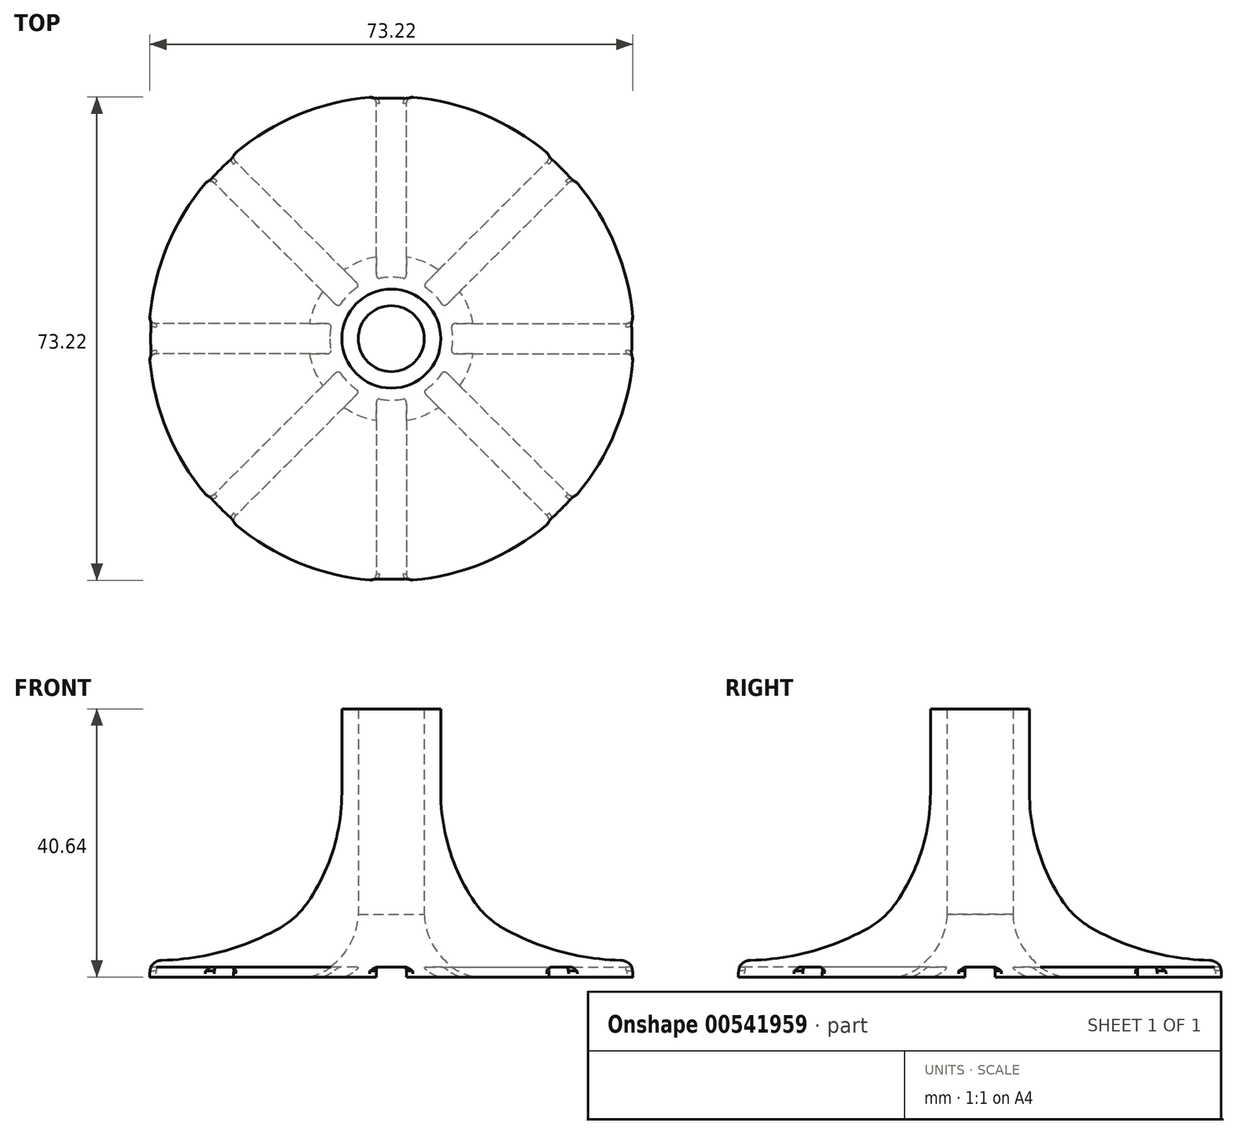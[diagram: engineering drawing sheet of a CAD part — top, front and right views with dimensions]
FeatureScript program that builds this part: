
annotation { "Feature Type Name" : "Feature", "Feature Type Description" : "" }
export const myFeature = defineFeature(function(context is Context, id is Id, definition is map)
    precondition{}
    {
        {
            var Q0;
            Q0=qCreatedBy(makeId("Front.planeOp"),FACE);
            var sketch = newSketch(context, id + "F0", { "sketchPlane" : qUnion([Q0])});
            skLineSegment(sketch, "E0", {"start": v(-7.5, 38.1) * mm, "end": v(-5, 38.1) * mm});
            skLineSegment(sketch, "E1", {"start": v(-5, 38.1) * mm, "end": v(-5, 0) * mm});
            skLineSegment(sketch, "E2", {"start": v(7.5, 38.1) * mm, "end": v(5, 38.1) * mm});
            skLineSegment(sketch, "E3", {"start": v(5, 38.1) * mm, "end": v(5, 0) * mm});
            skLineSegment(sketch, "E4", {"start": v(-7.5, 38.1) * mm, "end": v(-7.5, 25.4) * mm});
            skLineSegment(sketch, "E5", {"start": v(7.5, 38.1) * mm, "end": v(7.5, 25.4) * mm});
            skArc(sketch, "E6", {"start": v(-14.53, 6.35) * mm, "mid": v(-9.31, 15.25) * mm, "end": v(-7.5, 25.4) * mm});
            skArc(sketch, "E7", {"start": v(7.5, 25.4) * mm, "mid": v(9.31, 15.25) * mm, "end": v(14.53, 6.35) * mm});
            skArc(sketch, "E8", {"start": v(-36.75, 0) * mm, "mid": v(-25.14, 1.45) * mm, "end": v(-14.52, 6.35) * mm});
            skArc(sketch, "E9", {"start": v(14.52, 6.35) * mm, "mid": v(25.14, 1.45) * mm, "end": v(36.75, 0) * mm});
            skLineSegment(sketch, "E10", {"start": v(-36.75, 0) * mm, "end": v(-36.75, -2.54) * mm});
            skLineSegment(sketch, "E11", {"start": v(-36.75, -2.54) * mm, "end": v(-5, -2.54) * mm});
            skLineSegment(sketch, "E12", {"start": v(5, 0) * mm, "end": v(5, -2.54) * mm});
            skLineSegment(sketch, "E13", {"start": v(5, -2.54) * mm, "end": v(36.75, -2.54) * mm});
            skLineSegment(sketch, "E14", {"start": v(36.75, -2.54) * mm, "end": v(36.75, 0) * mm});
            skLineSegment(sketch, "E15", {"start": v(-5, -2.54) * mm, "end": v(-5, 0) * mm});
            skLineSegment(sketch, "E16", {"start": v(0, 0) * mm, "end": v(0, 88.81) * mm});
            skArc(sketch, "E17", {"start": v(-12.62, -2.54) * mm, "mid": v(-7.03, 1.2) * mm, "end": v(-5, 7.62) * mm});
            skSolve(sketch);
        }
        {
            var Q0;
            Q0=makeQuery(id+"F0.imprint","IMPRINT",FACE,{"disambiguationData":[TD([[makeQuery(id+"F0.imprint","IMPRINT",EDGE,{"derivedFrom":sQuery(id+"F0.wireOp",EDGE,"E0")}),-1.0]])]});
            var Q1;
            Q1=sQuery(id+"F0.wireOp",EDGE,"E16");
            revolve(context, id + "F1", {"entities" : qUnion([Q0]), "axis" : qUnion([Q1]), "revolveType" : RevolveType.FULL});
        }
        {
            var Q0;
            Q0=makeQuery(id+"F1.opRevolve","SWEPT_FACE",FACE,{"disambiguationData":[OSD([sQuery(id+"F0.wireOp",EDGE,"E11")])]});
            var sketch = newSketch(context, id + "F2", { "sketchPlane" : qUnion([Q0])});
            skLineSegment(sketch, "E18", {"start": v(0, 0) * mm, "end": v(40.46, 0) * mm});
            skLineSegment(sketch, "E19", {"start": v(0, 0) * mm, "end": v(-39.43, 0) * mm});
            skLineSegment(sketch, "E20", {"start": v(0, 0) * mm, "end": v(0, 40.5) * mm});
            skLineSegment(sketch, "E21", {"start": v(0, 0) * mm, "end": v(0, -43.24) * mm});
            skLineSegment(sketch, "E22", {"start": v(0, 0) * mm, "end": v(-31.82, 31.82) * mm});
            skLineSegment(sketch, "E23", {"start": v(0, 0) * mm, "end": v(30.6, 30.6) * mm});
            skLineSegment(sketch, "E24", {"start": v(0, 0) * mm, "end": v(-30.28, -30.28) * mm});
            skLineSegment(sketch, "E25", {"start": v(0, 0) * mm, "end": v(33.13, -33.13) * mm});
            skLineSegment(sketch, "E26.0", {"start": v(-5.52, 2.29) * mm, "end": v(-33.44, 30.2) * mm});
            skLineSegment(sketch, "E26.1", {"start": v(-5.52, 2.29) * mm, "end": v(-39.43, 2.29) * mm});
            skLineSegment(sketch, "E27.0", {"start": v(-2.29, 5.52) * mm, "end": v(-30.2, 33.44) * mm});
            skLineSegment(sketch, "E27.1", {"start": v(-2.29, 5.52) * mm, "end": v(-2.29, 40.5) * mm});
            skLineSegment(sketch, "E28.0", {"start": v(2.29, 5.52) * mm, "end": v(2.29, 40.5) * mm});
            skLineSegment(sketch, "E28.1", {"start": v(2.29, 5.52) * mm, "end": v(28.99, 32.22) * mm});
            skLineSegment(sketch, "E29.0", {"start": v(5.52, 2.29) * mm, "end": v(32.22, 28.99) * mm});
            skLineSegment(sketch, "E29.1", {"start": v(5.52, 2.29) * mm, "end": v(40.46, 2.29) * mm});
            skLineSegment(sketch, "E30.0", {"start": v(5.52, -2.29) * mm, "end": v(40.46, -2.29) * mm});
            skLineSegment(sketch, "E30.1", {"start": v(5.52, -2.29) * mm, "end": v(34.75, -31.52) * mm});
            skLineSegment(sketch, "E31.0", {"start": v(2.29, -5.52) * mm, "end": v(2.29, -43.24) * mm});
            skLineSegment(sketch, "E31.1", {"start": v(2.29, -5.52) * mm, "end": v(31.52, -34.75) * mm});
            skLineSegment(sketch, "E32.0", {"start": v(-2.29, -5.52) * mm, "end": v(-28.67, -31.9) * mm});
            skLineSegment(sketch, "E32.1", {"start": v(-2.29, -5.52) * mm, "end": v(-2.29, -43.24) * mm});
            skLineSegment(sketch, "E33.0", {"start": v(-5.52, -2.29) * mm, "end": v(-31.9, -28.67) * mm});
            skLineSegment(sketch, "E33.1", {"start": v(-5.52, -2.29) * mm, "end": v(-39.43, -2.29) * mm});
            skSolve(sketch);
        }
        {
            var Q0;
            {var subQ0=sQuery(id+"F2.wireOp",EDGE,"E26.1");var subQ1=sQuery(id+"F2.wireOp",EDGE,"E26.0");var subQ2=makeQuery(id+"F2.imprint","INTERSECT",VERTEX,{"derivedFrom":[subQ1,subQ0]});Q0=makeQuery(id+"F2.imprint","IMPRINT",FACE,{"disambiguationData":[TD([[makeQuery(id+"F2.imprint","IMPRINT",EDGE,{"disambiguationData":[TD([[subQ2,-1.0]])],"derivedFrom":subQ1}),-1.0]])]});}
            var Q1;
            {var subQ0=sQuery(id+"F2.wireOp",EDGE,"E27.1");var subQ1=sQuery(id+"F2.wireOp",EDGE,"E27.0");var subQ2=makeQuery(id+"F2.imprint","INTERSECT",VERTEX,{"derivedFrom":[subQ1,subQ0]});Q1=makeQuery(id+"F2.imprint","IMPRINT",FACE,{"disambiguationData":[TD([[makeQuery(id+"F2.imprint","IMPRINT",EDGE,{"disambiguationData":[TD([[subQ2,-1.0]])],"derivedFrom":subQ1}),1.0]])]});}
            var Q2;
            {var subQ0=sQuery(id+"F2.wireOp",EDGE,"E28.1");var subQ1=sQuery(id+"F2.wireOp",EDGE,"E28.0");var subQ2=makeQuery(id+"F2.imprint","INTERSECT",VERTEX,{"derivedFrom":[subQ1,subQ0]});Q2=makeQuery(id+"F2.imprint","IMPRINT",FACE,{"disambiguationData":[TD([[makeQuery(id+"F2.imprint","IMPRINT",EDGE,{"disambiguationData":[TD([[subQ2,-1.0]])],"derivedFrom":subQ1}),1.0]])]});}
            var Q3;
            {var subQ0=sQuery(id+"F2.wireOp",EDGE,"E29.1");var subQ1=sQuery(id+"F2.wireOp",EDGE,"E29.0");var subQ2=makeQuery(id+"F2.imprint","INTERSECT",VERTEX,{"derivedFrom":[subQ1,subQ0]});Q3=makeQuery(id+"F2.imprint","IMPRINT",FACE,{"disambiguationData":[TD([[makeQuery(id+"F2.imprint","IMPRINT",EDGE,{"disambiguationData":[TD([[subQ2,-1.0]])],"derivedFrom":subQ1}),1.0]])]});}
            var Q4;
            {var subQ0=sQuery(id+"F2.wireOp",EDGE,"E30.1");var subQ1=sQuery(id+"F2.wireOp",EDGE,"E30.0");var subQ2=makeQuery(id+"F2.imprint","INTERSECT",VERTEX,{"derivedFrom":[subQ1,subQ0]});Q4=makeQuery(id+"F2.imprint","IMPRINT",FACE,{"disambiguationData":[TD([[makeQuery(id+"F2.imprint","IMPRINT",EDGE,{"disambiguationData":[TD([[subQ2,-1.0]])],"derivedFrom":subQ1}),1.0]])]});}
            var Q5;
            {var subQ0=sQuery(id+"F2.wireOp",EDGE,"E31.1");var subQ1=sQuery(id+"F2.wireOp",EDGE,"E31.0");var subQ2=makeQuery(id+"F2.imprint","INTERSECT",VERTEX,{"derivedFrom":[subQ1,subQ0]});Q5=makeQuery(id+"F2.imprint","IMPRINT",FACE,{"disambiguationData":[TD([[makeQuery(id+"F2.imprint","IMPRINT",EDGE,{"disambiguationData":[TD([[subQ2,-1.0]])],"derivedFrom":subQ1}),-1.0]])]});}
            var Q6;
            {var subQ0=sQuery(id+"F2.wireOp",EDGE,"E32.1");var subQ1=sQuery(id+"F2.wireOp",EDGE,"E32.0");var subQ2=makeQuery(id+"F2.imprint","INTERSECT",VERTEX,{"derivedFrom":[subQ1,subQ0]});Q6=makeQuery(id+"F2.imprint","IMPRINT",FACE,{"disambiguationData":[TD([[makeQuery(id+"F2.imprint","IMPRINT",EDGE,{"disambiguationData":[TD([[subQ2,-1.0]])],"derivedFrom":subQ1}),-1.0]])]});}
            var Q7;
            {var subQ0=sQuery(id+"F2.wireOp",EDGE,"E33.1");var subQ1=sQuery(id+"F2.wireOp",EDGE,"E33.0");var subQ2=makeQuery(id+"F2.imprint","INTERSECT",VERTEX,{"derivedFrom":[subQ1,subQ0]});Q7=makeQuery(id+"F2.imprint","IMPRINT",FACE,{"disambiguationData":[TD([[makeQuery(id+"F2.imprint","IMPRINT",EDGE,{"disambiguationData":[TD([[subQ2,-1.0]])],"derivedFrom":subQ1}),1.0]])]});}
            var Q8;
            {var subQ0=sQuery(id+"F2.wireOp",EDGE,"E22");var subQ1=sQuery(id+"F0.wireOp",EDGE,"E11");var subQ2=makeQuery(id+"F1.opRevolve","SWEPT_EDGE",EDGE,{"disambiguationData":[OSD([sQuery(id+"F0.wireOp",EDGE,"E10"),subQ1])]});var subQ3=makeQuery(id+"F2.imprint","INTERSECT",VERTEX,{"derivedFrom":[subQ2,subQ0]});Q8=makeQuery(id+"F2.imprint","IMPRINT",FACE,{"disambiguationData":[TD([[makeQuery(id+"F2.imprint","IMPRINT",EDGE,{"disambiguationData":[TD([[subQ3,1.0]])],"derivedFrom":subQ0}),1.0]])]});}
            var Q9;
            {var subQ0=sQuery(id+"F2.wireOp",EDGE,"E22");var subQ1=sQuery(id+"F0.wireOp",EDGE,"E11");var subQ2=makeQuery(id+"F1.opRevolve","SWEPT_EDGE",EDGE,{"disambiguationData":[OSD([sQuery(id+"F0.wireOp",EDGE,"E10"),subQ1])]});var subQ3=makeQuery(id+"F2.imprint","INTERSECT",VERTEX,{"derivedFrom":[subQ2,subQ0]});Q9=makeQuery(id+"F2.imprint","IMPRINT",FACE,{"disambiguationData":[TD([[makeQuery(id+"F2.imprint","IMPRINT",EDGE,{"disambiguationData":[TD([[subQ3,1.0]])],"derivedFrom":subQ0}),-1.0]])]});}
            var Q10;
            {var subQ0=sQuery(id+"F2.wireOp",EDGE,"E20");var subQ1=sQuery(id+"F0.wireOp",EDGE,"E11");var subQ2=makeQuery(id+"F1.opRevolve","SWEPT_EDGE",EDGE,{"disambiguationData":[OSD([sQuery(id+"F0.wireOp",EDGE,"E10"),subQ1])]});var subQ3=makeQuery(id+"F2.imprint","INTERSECT",VERTEX,{"derivedFrom":[subQ2,subQ0]});Q10=makeQuery(id+"F2.imprint","IMPRINT",FACE,{"disambiguationData":[TD([[makeQuery(id+"F2.imprint","IMPRINT",EDGE,{"disambiguationData":[TD([[subQ3,1.0]])],"derivedFrom":subQ0}),1.0]])]});}
            var Q11;
            {var subQ0=sQuery(id+"F2.wireOp",EDGE,"E20");var subQ1=sQuery(id+"F0.wireOp",EDGE,"E11");var subQ2=makeQuery(id+"F1.opRevolve","SWEPT_EDGE",EDGE,{"disambiguationData":[OSD([sQuery(id+"F0.wireOp",EDGE,"E10"),subQ1])]});var subQ3=makeQuery(id+"F2.imprint","INTERSECT",VERTEX,{"derivedFrom":[subQ2,subQ0]});Q11=makeQuery(id+"F2.imprint","IMPRINT",FACE,{"disambiguationData":[TD([[makeQuery(id+"F2.imprint","IMPRINT",EDGE,{"disambiguationData":[TD([[subQ3,1.0]])],"derivedFrom":subQ0}),-1.0]])]});}
            var Q12;
            {var subQ0=sQuery(id+"F2.wireOp",EDGE,"E23");var subQ1=sQuery(id+"F0.wireOp",EDGE,"E11");var subQ2=makeQuery(id+"F1.opRevolve","SWEPT_EDGE",EDGE,{"disambiguationData":[OSD([sQuery(id+"F0.wireOp",EDGE,"E10"),subQ1])]});var subQ3=makeQuery(id+"F2.imprint","INTERSECT",VERTEX,{"derivedFrom":[subQ2,subQ0]});Q12=makeQuery(id+"F2.imprint","IMPRINT",FACE,{"disambiguationData":[TD([[makeQuery(id+"F2.imprint","IMPRINT",EDGE,{"disambiguationData":[TD([[subQ3,1.0]])],"derivedFrom":subQ0}),1.0]])]});}
            var Q13;
            {var subQ0=sQuery(id+"F2.wireOp",EDGE,"E23");var subQ1=sQuery(id+"F0.wireOp",EDGE,"E11");var subQ2=makeQuery(id+"F1.opRevolve","SWEPT_EDGE",EDGE,{"disambiguationData":[OSD([sQuery(id+"F0.wireOp",EDGE,"E10"),subQ1])]});var subQ3=makeQuery(id+"F2.imprint","INTERSECT",VERTEX,{"derivedFrom":[subQ2,subQ0]});Q13=makeQuery(id+"F2.imprint","IMPRINT",FACE,{"disambiguationData":[TD([[makeQuery(id+"F2.imprint","IMPRINT",EDGE,{"disambiguationData":[TD([[subQ3,1.0]])],"derivedFrom":subQ0}),-1.0]])]});}
            var Q14;
            {var subQ0=sQuery(id+"F2.wireOp",EDGE,"E18");var subQ1=sQuery(id+"F0.wireOp",EDGE,"E11");var subQ2=makeQuery(id+"F1.opRevolve","SWEPT_EDGE",EDGE,{"disambiguationData":[OSD([sQuery(id+"F0.wireOp",EDGE,"E10"),subQ1])]});var subQ3=makeQuery(id+"F2.imprint","INTERSECT",VERTEX,{"derivedFrom":[subQ2,subQ0]});Q14=makeQuery(id+"F2.imprint","IMPRINT",FACE,{"disambiguationData":[TD([[makeQuery(id+"F2.imprint","IMPRINT",EDGE,{"disambiguationData":[TD([[subQ3,1.0]])],"derivedFrom":subQ0}),1.0]])]});}
            var Q15;
            {var subQ0=sQuery(id+"F2.wireOp",EDGE,"E18");var subQ1=sQuery(id+"F0.wireOp",EDGE,"E11");var subQ2=makeQuery(id+"F1.opRevolve","SWEPT_EDGE",EDGE,{"disambiguationData":[OSD([sQuery(id+"F0.wireOp",EDGE,"E10"),subQ1])]});var subQ3=makeQuery(id+"F2.imprint","INTERSECT",VERTEX,{"derivedFrom":[subQ2,subQ0]});Q15=makeQuery(id+"F2.imprint","IMPRINT",FACE,{"disambiguationData":[TD([[makeQuery(id+"F2.imprint","IMPRINT",EDGE,{"disambiguationData":[TD([[subQ3,1.0]])],"derivedFrom":subQ0}),-1.0]])]});}
            var Q16;
            {var subQ0=sQuery(id+"F2.wireOp",EDGE,"E25");var subQ1=sQuery(id+"F0.wireOp",EDGE,"E11");var subQ2=makeQuery(id+"F1.opRevolve","SWEPT_EDGE",EDGE,{"disambiguationData":[OSD([sQuery(id+"F0.wireOp",EDGE,"E10"),subQ1])]});var subQ3=makeQuery(id+"F2.imprint","INTERSECT",VERTEX,{"derivedFrom":[subQ2,subQ0]});Q16=makeQuery(id+"F2.imprint","IMPRINT",FACE,{"disambiguationData":[TD([[makeQuery(id+"F2.imprint","IMPRINT",EDGE,{"disambiguationData":[TD([[subQ3,1.0]])],"derivedFrom":subQ0}),1.0]])]});}
            var Q17;
            {var subQ0=sQuery(id+"F2.wireOp",EDGE,"E25");var subQ1=sQuery(id+"F0.wireOp",EDGE,"E11");var subQ2=makeQuery(id+"F1.opRevolve","SWEPT_EDGE",EDGE,{"disambiguationData":[OSD([sQuery(id+"F0.wireOp",EDGE,"E10"),subQ1])]});var subQ3=makeQuery(id+"F2.imprint","INTERSECT",VERTEX,{"derivedFrom":[subQ2,subQ0]});Q17=makeQuery(id+"F2.imprint","IMPRINT",FACE,{"disambiguationData":[TD([[makeQuery(id+"F2.imprint","IMPRINT",EDGE,{"disambiguationData":[TD([[subQ3,1.0]])],"derivedFrom":subQ0}),-1.0]])]});}
            var Q18;
            {var subQ0=sQuery(id+"F2.wireOp",EDGE,"E21");var subQ1=sQuery(id+"F0.wireOp",EDGE,"E11");var subQ2=makeQuery(id+"F1.opRevolve","SWEPT_EDGE",EDGE,{"disambiguationData":[OSD([sQuery(id+"F0.wireOp",EDGE,"E10"),subQ1])]});var subQ3=makeQuery(id+"F2.imprint","INTERSECT",VERTEX,{"derivedFrom":[subQ2,subQ0]});Q18=makeQuery(id+"F2.imprint","IMPRINT",FACE,{"disambiguationData":[TD([[makeQuery(id+"F2.imprint","IMPRINT",EDGE,{"disambiguationData":[TD([[subQ3,1.0]])],"derivedFrom":subQ0}),1.0]])]});}
            var Q19;
            {var subQ0=sQuery(id+"F2.wireOp",EDGE,"E21");var subQ1=sQuery(id+"F0.wireOp",EDGE,"E11");var subQ2=makeQuery(id+"F1.opRevolve","SWEPT_EDGE",EDGE,{"disambiguationData":[OSD([sQuery(id+"F0.wireOp",EDGE,"E10"),subQ1])]});var subQ3=makeQuery(id+"F2.imprint","INTERSECT",VERTEX,{"derivedFrom":[subQ2,subQ0]});Q19=makeQuery(id+"F2.imprint","IMPRINT",FACE,{"disambiguationData":[TD([[makeQuery(id+"F2.imprint","IMPRINT",EDGE,{"disambiguationData":[TD([[subQ3,1.0]])],"derivedFrom":subQ0}),-1.0]])]});}
            var Q20;
            {var subQ0=sQuery(id+"F2.wireOp",EDGE,"E24");var subQ1=sQuery(id+"F0.wireOp",EDGE,"E11");var subQ2=makeQuery(id+"F1.opRevolve","SWEPT_EDGE",EDGE,{"disambiguationData":[OSD([sQuery(id+"F0.wireOp",EDGE,"E10"),subQ1])]});var subQ3=makeQuery(id+"F2.imprint","INTERSECT",VERTEX,{"derivedFrom":[subQ2,subQ0]});Q20=makeQuery(id+"F2.imprint","IMPRINT",FACE,{"disambiguationData":[TD([[makeQuery(id+"F2.imprint","IMPRINT",EDGE,{"disambiguationData":[TD([[subQ3,1.0]])],"derivedFrom":subQ0}),1.0]])]});}
            var Q21;
            {var subQ0=sQuery(id+"F2.wireOp",EDGE,"E24");var subQ1=sQuery(id+"F0.wireOp",EDGE,"E11");var subQ2=makeQuery(id+"F1.opRevolve","SWEPT_EDGE",EDGE,{"disambiguationData":[OSD([sQuery(id+"F0.wireOp",EDGE,"E10"),subQ1])]});var subQ3=makeQuery(id+"F2.imprint","INTERSECT",VERTEX,{"derivedFrom":[subQ2,subQ0]});Q21=makeQuery(id+"F2.imprint","IMPRINT",FACE,{"disambiguationData":[TD([[makeQuery(id+"F2.imprint","IMPRINT",EDGE,{"disambiguationData":[TD([[subQ3,1.0]])],"derivedFrom":subQ0}),-1.0]])]});}
            var Q22;
            {var subQ0=sQuery(id+"F2.wireOp",EDGE,"E19");var subQ1=sQuery(id+"F0.wireOp",EDGE,"E11");var subQ2=makeQuery(id+"F1.opRevolve","SWEPT_EDGE",EDGE,{"disambiguationData":[OSD([sQuery(id+"F0.wireOp",EDGE,"E10"),subQ1])]});var subQ3=makeQuery(id+"F2.imprint","INTERSECT",VERTEX,{"derivedFrom":[subQ2,subQ0]});Q22=makeQuery(id+"F2.imprint","IMPRINT",FACE,{"disambiguationData":[TD([[makeQuery(id+"F2.imprint","IMPRINT",EDGE,{"disambiguationData":[TD([[subQ3,1.0]])],"derivedFrom":subQ0}),1.0]])]});}
            var Q23;
            {var subQ0=sQuery(id+"F2.wireOp",EDGE,"E19");var subQ1=sQuery(id+"F0.wireOp",EDGE,"E11");var subQ2=makeQuery(id+"F1.opRevolve","SWEPT_EDGE",EDGE,{"disambiguationData":[OSD([sQuery(id+"F0.wireOp",EDGE,"E10"),subQ1])]});var subQ3=makeQuery(id+"F2.imprint","INTERSECT",VERTEX,{"derivedFrom":[subQ2,subQ0]});Q23=makeQuery(id+"F2.imprint","IMPRINT",FACE,{"disambiguationData":[TD([[makeQuery(id+"F2.imprint","IMPRINT",EDGE,{"disambiguationData":[TD([[subQ3,1.0]])],"derivedFrom":subQ0}),-1.0]])]});}
            extrude(context, id + "F3", {"entities" : qUnion([Q0, Q1, Q2, Q3, Q4, Q5, Q6, Q7, Q8, Q9, Q10, Q11, Q12, Q13, Q14, Q15, Q16, Q17, Q18, Q19, Q20, Q21, Q22, Q23]), "operationType" : NewBodyOperationType.REMOVE, "oppositeDirection" : true, "depth" : 1.52 * mm, "offsetDistance" : 25.4 * mm});
        }
        {
            var Q0;
            Q0=makeQuery(id+"F1.opRevolve","SWEPT_EDGE",EDGE,{"disambiguationData":[OSD([sQuery(id+"F0.wireOp",EDGE,"E8"),sQuery(id+"F0.wireOp",EDGE,"E10")])]});
            fillet(context, id + "F4", {"entities" : qUnion([Q0]), "radius" : 2.03 * mm, "tangentPropagation" : true, "allowEdgeOverflow" : false});
        }
        {
            var Q0;
            Q0=makeQuery(id+"F1.opRevolve","SWEPT_EDGE",EDGE,{"disambiguationData":[OSD([sQuery(id+"F0.wireOp",EDGE,"E6"),sQuery(id+"F0.wireOp",EDGE,"E8")])]});
            fillet(context, id + "F5", {"entities" : qUnion([Q0]), "radius" : 12.7 * mm, "tangentPropagation" : true, "allowEdgeOverflow" : false});
        }
        {
            var Q0;
            Q0=makeQuery(id+"F4.opFillet","BLEND_EDGE",EDGE,{"blendedFrom":[makeQuery(id+"F1.opRevolve","SWEPT_EDGE",EDGE,{"disambiguationData":[OSD([sQuery(id+"F0.wireOp",EDGE,"E8"),sQuery(id+"F0.wireOp",EDGE,"E10")])]}),makeQuery(id+"F3.boolean.opBoolean","COPY",FACE,{"derivedFrom":makeQuery(id+"F3.opExtrude","SWEPT_FACE",FACE,{"disambiguationData":[OSD([sQuery(id+"F2.wireOp",EDGE,"E27.0")])]})})],"blendedInto":[makeQuery(id+"F3.boolean.opBoolean","COPY",FACE,{"derivedFrom":makeQuery(id+"F3.opExtrude","SWEPT_FACE",FACE,{"disambiguationData":[OSD([sQuery(id+"F2.wireOp",EDGE,"E27.0")])]})})]});
            var Q1;
            Q1=makeQuery(id+"F4.opFillet","BLEND_EDGE",EDGE,{"blendedFrom":[makeQuery(id+"F1.opRevolve","SWEPT_EDGE",EDGE,{"disambiguationData":[OSD([sQuery(id+"F0.wireOp",EDGE,"E8"),sQuery(id+"F0.wireOp",EDGE,"E10")])]}),makeQuery(id+"F3.boolean.opBoolean","COPY",FACE,{"derivedFrom":makeQuery(id+"F3.opExtrude","SWEPT_FACE",FACE,{"disambiguationData":[OSD([sQuery(id+"F2.wireOp",EDGE,"E26.0")])]})})],"blendedInto":[makeQuery(id+"F3.boolean.opBoolean","COPY",FACE,{"derivedFrom":makeQuery(id+"F3.opExtrude","SWEPT_FACE",FACE,{"disambiguationData":[OSD([sQuery(id+"F2.wireOp",EDGE,"E26.0")])]})})]});
            var Q2;
            Q2=makeQuery(id+"F4.opFillet","BLEND_EDGE",EDGE,{"blendedFrom":[makeQuery(id+"F1.opRevolve","SWEPT_EDGE",EDGE,{"disambiguationData":[OSD([sQuery(id+"F0.wireOp",EDGE,"E8"),sQuery(id+"F0.wireOp",EDGE,"E10")])]}),makeQuery(id+"F3.boolean.opBoolean","COPY",FACE,{"derivedFrom":makeQuery(id+"F3.opExtrude","SWEPT_FACE",FACE,{"disambiguationData":[OSD([sQuery(id+"F2.wireOp",EDGE,"E28.0")])]})})],"blendedInto":[makeQuery(id+"F3.boolean.opBoolean","COPY",FACE,{"derivedFrom":makeQuery(id+"F3.opExtrude","SWEPT_FACE",FACE,{"disambiguationData":[OSD([sQuery(id+"F2.wireOp",EDGE,"E28.0")])]})})]});
            var Q3;
            Q3=makeQuery(id+"F4.opFillet","BLEND_EDGE",EDGE,{"blendedFrom":[makeQuery(id+"F1.opRevolve","SWEPT_EDGE",EDGE,{"disambiguationData":[OSD([sQuery(id+"F0.wireOp",EDGE,"E8"),sQuery(id+"F0.wireOp",EDGE,"E10")])]}),makeQuery(id+"F3.boolean.opBoolean","COPY",FACE,{"derivedFrom":makeQuery(id+"F3.opExtrude","SWEPT_FACE",FACE,{"disambiguationData":[OSD([sQuery(id+"F2.wireOp",EDGE,"E27.1")])]})})],"blendedInto":[makeQuery(id+"F3.boolean.opBoolean","COPY",FACE,{"derivedFrom":makeQuery(id+"F3.opExtrude","SWEPT_FACE",FACE,{"disambiguationData":[OSD([sQuery(id+"F2.wireOp",EDGE,"E27.1")])]})})]});
            var Q4;
            Q4=makeQuery(id+"F4.opFillet","BLEND_EDGE",EDGE,{"blendedFrom":[makeQuery(id+"F1.opRevolve","SWEPT_EDGE",EDGE,{"disambiguationData":[OSD([sQuery(id+"F0.wireOp",EDGE,"E8"),sQuery(id+"F0.wireOp",EDGE,"E10")])]}),makeQuery(id+"F3.boolean.opBoolean","COPY",FACE,{"derivedFrom":makeQuery(id+"F3.opExtrude","SWEPT_FACE",FACE,{"disambiguationData":[OSD([sQuery(id+"F2.wireOp",EDGE,"E29.0")])]})})],"blendedInto":[makeQuery(id+"F3.boolean.opBoolean","COPY",FACE,{"derivedFrom":makeQuery(id+"F3.opExtrude","SWEPT_FACE",FACE,{"disambiguationData":[OSD([sQuery(id+"F2.wireOp",EDGE,"E29.0")])]})})]});
            var Q5;
            Q5=makeQuery(id+"F4.opFillet","BLEND_EDGE",EDGE,{"blendedFrom":[makeQuery(id+"F1.opRevolve","SWEPT_EDGE",EDGE,{"disambiguationData":[OSD([sQuery(id+"F0.wireOp",EDGE,"E8"),sQuery(id+"F0.wireOp",EDGE,"E10")])]}),makeQuery(id+"F3.boolean.opBoolean","COPY",FACE,{"derivedFrom":makeQuery(id+"F3.opExtrude","SWEPT_FACE",FACE,{"disambiguationData":[OSD([sQuery(id+"F2.wireOp",EDGE,"E28.1")])]})})],"blendedInto":[makeQuery(id+"F3.boolean.opBoolean","COPY",FACE,{"derivedFrom":makeQuery(id+"F3.opExtrude","SWEPT_FACE",FACE,{"disambiguationData":[OSD([sQuery(id+"F2.wireOp",EDGE,"E28.1")])]})})]});
            var Q6;
            Q6=makeQuery(id+"F4.opFillet","BLEND_EDGE",EDGE,{"blendedFrom":[makeQuery(id+"F1.opRevolve","SWEPT_EDGE",EDGE,{"disambiguationData":[OSD([sQuery(id+"F0.wireOp",EDGE,"E8"),sQuery(id+"F0.wireOp",EDGE,"E10")])]}),makeQuery(id+"F3.boolean.opBoolean","COPY",FACE,{"derivedFrom":makeQuery(id+"F3.opExtrude","SWEPT_FACE",FACE,{"disambiguationData":[OSD([sQuery(id+"F2.wireOp",EDGE,"E30.0")])]})})],"blendedInto":[makeQuery(id+"F3.boolean.opBoolean","COPY",FACE,{"derivedFrom":makeQuery(id+"F3.opExtrude","SWEPT_FACE",FACE,{"disambiguationData":[OSD([sQuery(id+"F2.wireOp",EDGE,"E30.0")])]})})]});
            var Q7;
            Q7=makeQuery(id+"F4.opFillet","BLEND_EDGE",EDGE,{"blendedFrom":[makeQuery(id+"F1.opRevolve","SWEPT_EDGE",EDGE,{"disambiguationData":[OSD([sQuery(id+"F0.wireOp",EDGE,"E8"),sQuery(id+"F0.wireOp",EDGE,"E10")])]}),makeQuery(id+"F3.boolean.opBoolean","COPY",FACE,{"derivedFrom":makeQuery(id+"F3.opExtrude","SWEPT_FACE",FACE,{"disambiguationData":[OSD([sQuery(id+"F2.wireOp",EDGE,"E29.1")])]})})],"blendedInto":[makeQuery(id+"F3.boolean.opBoolean","COPY",FACE,{"derivedFrom":makeQuery(id+"F3.opExtrude","SWEPT_FACE",FACE,{"disambiguationData":[OSD([sQuery(id+"F2.wireOp",EDGE,"E29.1")])]})})]});
            var Q8;
            Q8=makeQuery(id+"F4.opFillet","BLEND_EDGE",EDGE,{"blendedFrom":[makeQuery(id+"F1.opRevolve","SWEPT_EDGE",EDGE,{"disambiguationData":[OSD([sQuery(id+"F0.wireOp",EDGE,"E8"),sQuery(id+"F0.wireOp",EDGE,"E10")])]}),makeQuery(id+"F3.boolean.opBoolean","COPY",FACE,{"derivedFrom":makeQuery(id+"F3.opExtrude","SWEPT_FACE",FACE,{"disambiguationData":[OSD([sQuery(id+"F2.wireOp",EDGE,"E30.1")])]})})],"blendedInto":[makeQuery(id+"F3.boolean.opBoolean","COPY",FACE,{"derivedFrom":makeQuery(id+"F3.opExtrude","SWEPT_FACE",FACE,{"disambiguationData":[OSD([sQuery(id+"F2.wireOp",EDGE,"E30.1")])]})})]});
            var Q9;
            Q9=makeQuery(id+"F4.opFillet","BLEND_EDGE",EDGE,{"blendedFrom":[makeQuery(id+"F1.opRevolve","SWEPT_EDGE",EDGE,{"disambiguationData":[OSD([sQuery(id+"F0.wireOp",EDGE,"E8"),sQuery(id+"F0.wireOp",EDGE,"E10")])]}),makeQuery(id+"F3.boolean.opBoolean","COPY",FACE,{"derivedFrom":makeQuery(id+"F3.opExtrude","SWEPT_FACE",FACE,{"disambiguationData":[OSD([sQuery(id+"F2.wireOp",EDGE,"E31.1")])]})})],"blendedInto":[makeQuery(id+"F3.boolean.opBoolean","COPY",FACE,{"derivedFrom":makeQuery(id+"F3.opExtrude","SWEPT_FACE",FACE,{"disambiguationData":[OSD([sQuery(id+"F2.wireOp",EDGE,"E31.1")])]})})]});
            var Q10;
            Q10=makeQuery(id+"F4.opFillet","BLEND_EDGE",EDGE,{"blendedFrom":[makeQuery(id+"F1.opRevolve","SWEPT_EDGE",EDGE,{"disambiguationData":[OSD([sQuery(id+"F0.wireOp",EDGE,"E8"),sQuery(id+"F0.wireOp",EDGE,"E10")])]}),makeQuery(id+"F3.boolean.opBoolean","COPY",FACE,{"derivedFrom":makeQuery(id+"F3.opExtrude","SWEPT_FACE",FACE,{"disambiguationData":[OSD([sQuery(id+"F2.wireOp",EDGE,"E31.0")])]})})],"blendedInto":[makeQuery(id+"F3.boolean.opBoolean","COPY",FACE,{"derivedFrom":makeQuery(id+"F3.opExtrude","SWEPT_FACE",FACE,{"disambiguationData":[OSD([sQuery(id+"F2.wireOp",EDGE,"E31.0")])]})})]});
            var Q11;
            Q11=makeQuery(id+"F4.opFillet","BLEND_EDGE",EDGE,{"blendedFrom":[makeQuery(id+"F1.opRevolve","SWEPT_EDGE",EDGE,{"disambiguationData":[OSD([sQuery(id+"F0.wireOp",EDGE,"E8"),sQuery(id+"F0.wireOp",EDGE,"E10")])]}),makeQuery(id+"F3.boolean.opBoolean","COPY",FACE,{"derivedFrom":makeQuery(id+"F3.opExtrude","SWEPT_FACE",FACE,{"disambiguationData":[OSD([sQuery(id+"F2.wireOp",EDGE,"E32.1")])]})})],"blendedInto":[makeQuery(id+"F3.boolean.opBoolean","COPY",FACE,{"derivedFrom":makeQuery(id+"F3.opExtrude","SWEPT_FACE",FACE,{"disambiguationData":[OSD([sQuery(id+"F2.wireOp",EDGE,"E32.1")])]})})]});
            var Q12;
            Q12=makeQuery(id+"F4.opFillet","BLEND_EDGE",EDGE,{"blendedFrom":[makeQuery(id+"F1.opRevolve","SWEPT_EDGE",EDGE,{"disambiguationData":[OSD([sQuery(id+"F0.wireOp",EDGE,"E8"),sQuery(id+"F0.wireOp",EDGE,"E10")])]}),makeQuery(id+"F3.boolean.opBoolean","COPY",FACE,{"derivedFrom":makeQuery(id+"F3.opExtrude","SWEPT_FACE",FACE,{"disambiguationData":[OSD([sQuery(id+"F2.wireOp",EDGE,"E32.0")])]})})],"blendedInto":[makeQuery(id+"F3.boolean.opBoolean","COPY",FACE,{"derivedFrom":makeQuery(id+"F3.opExtrude","SWEPT_FACE",FACE,{"disambiguationData":[OSD([sQuery(id+"F2.wireOp",EDGE,"E32.0")])]})})]});
            var Q13;
            Q13=makeQuery(id+"F4.opFillet","BLEND_EDGE",EDGE,{"blendedFrom":[makeQuery(id+"F1.opRevolve","SWEPT_EDGE",EDGE,{"disambiguationData":[OSD([sQuery(id+"F0.wireOp",EDGE,"E8"),sQuery(id+"F0.wireOp",EDGE,"E10")])]}),makeQuery(id+"F3.boolean.opBoolean","COPY",FACE,{"derivedFrom":makeQuery(id+"F3.opExtrude","SWEPT_FACE",FACE,{"disambiguationData":[OSD([sQuery(id+"F2.wireOp",EDGE,"E33.0")])]})})],"blendedInto":[makeQuery(id+"F3.boolean.opBoolean","COPY",FACE,{"derivedFrom":makeQuery(id+"F3.opExtrude","SWEPT_FACE",FACE,{"disambiguationData":[OSD([sQuery(id+"F2.wireOp",EDGE,"E33.0")])]})})]});
            var Q14;
            Q14=makeQuery(id+"F4.opFillet","BLEND_EDGE",EDGE,{"blendedFrom":[makeQuery(id+"F1.opRevolve","SWEPT_EDGE",EDGE,{"disambiguationData":[OSD([sQuery(id+"F0.wireOp",EDGE,"E8"),sQuery(id+"F0.wireOp",EDGE,"E10")])]}),makeQuery(id+"F3.boolean.opBoolean","COPY",FACE,{"derivedFrom":makeQuery(id+"F3.opExtrude","SWEPT_FACE",FACE,{"disambiguationData":[OSD([sQuery(id+"F2.wireOp",EDGE,"E33.1")])]})})],"blendedInto":[makeQuery(id+"F3.boolean.opBoolean","COPY",FACE,{"derivedFrom":makeQuery(id+"F3.opExtrude","SWEPT_FACE",FACE,{"disambiguationData":[OSD([sQuery(id+"F2.wireOp",EDGE,"E33.1")])]})})]});
            var Q15;
            Q15=makeQuery(id+"F4.opFillet","BLEND_EDGE",EDGE,{"blendedFrom":[makeQuery(id+"F1.opRevolve","SWEPT_EDGE",EDGE,{"disambiguationData":[OSD([sQuery(id+"F0.wireOp",EDGE,"E8"),sQuery(id+"F0.wireOp",EDGE,"E10")])]}),makeQuery(id+"F3.boolean.opBoolean","COPY",FACE,{"derivedFrom":makeQuery(id+"F3.opExtrude","SWEPT_FACE",FACE,{"disambiguationData":[OSD([sQuery(id+"F2.wireOp",EDGE,"E26.1")])]})})],"blendedInto":[makeQuery(id+"F3.boolean.opBoolean","COPY",FACE,{"derivedFrom":makeQuery(id+"F3.opExtrude","SWEPT_FACE",FACE,{"disambiguationData":[OSD([sQuery(id+"F2.wireOp",EDGE,"E26.1")])]})})]});
            fillet(context, id + "F6", {"entities" : qUnion([Q0, Q1, Q2, Q3, Q4, Q5, Q6, Q7, Q8, Q9, Q10, Q11, Q12, Q13, Q14, Q15]), "radius" : 0.89 * mm, "tangentPropagation" : true, "allowEdgeOverflow" : false});
        }
        {
            var Q0;
            Q0=makeQuery(id+"F3.boolean.opBoolean","COPY",EDGE,{"derivedFrom":makeQuery(id+"F3.opExtrude","CAP_EDGE",EDGE,{"disambiguationData":[OSD([sQuery(id+"F2.wireOp",EDGE,"E32.1")])],"isStart":false})});
            var Q1;
            Q1=makeQuery(id+"F3.boolean.opBoolean","COPY",EDGE,{"derivedFrom":makeQuery(id+"F3.opExtrude","CAP_EDGE",EDGE,{"disambiguationData":[OSD([sQuery(id+"F2.wireOp",EDGE,"E31.0")])],"isStart":false})});
            var Q2;
            Q2=makeQuery(id+"F3.boolean.opBoolean","COPY",EDGE,{"derivedFrom":makeQuery(id+"F3.opExtrude","CAP_EDGE",EDGE,{"disambiguationData":[OSD([sQuery(id+"F2.wireOp",EDGE,"E33.0")])],"isStart":false})});
            var Q3;
            Q3=makeQuery(id+"F3.boolean.opBoolean","COPY",EDGE,{"derivedFrom":makeQuery(id+"F3.opExtrude","CAP_EDGE",EDGE,{"disambiguationData":[OSD([sQuery(id+"F2.wireOp",EDGE,"E32.0")])],"isStart":false})});
            var Q4;
            Q4=makeQuery(id+"F3.boolean.opBoolean","COPY",EDGE,{"derivedFrom":makeQuery(id+"F3.opExtrude","CAP_EDGE",EDGE,{"disambiguationData":[OSD([sQuery(id+"F2.wireOp",EDGE,"E31.1")])],"isStart":false})});
            var Q5;
            Q5=makeQuery(id+"F3.boolean.opBoolean","COPY",EDGE,{"derivedFrom":makeQuery(id+"F3.opExtrude","CAP_EDGE",EDGE,{"disambiguationData":[OSD([sQuery(id+"F2.wireOp",EDGE,"E33.1")])],"isStart":false})});
            var Q6;
            Q6=makeQuery(id+"F3.boolean.opBoolean","COPY",EDGE,{"derivedFrom":makeQuery(id+"F3.opExtrude","CAP_EDGE",EDGE,{"disambiguationData":[OSD([sQuery(id+"F2.wireOp",EDGE,"E26.0")])],"isStart":false})});
            var Q7;
            Q7=makeQuery(id+"F3.boolean.opBoolean","COPY",EDGE,{"derivedFrom":makeQuery(id+"F3.opExtrude","CAP_EDGE",EDGE,{"disambiguationData":[OSD([sQuery(id+"F2.wireOp",EDGE,"E27.1")])],"isStart":false})});
            var Q8;
            Q8=makeQuery(id+"F3.boolean.opBoolean","COPY",EDGE,{"derivedFrom":makeQuery(id+"F3.opExtrude","CAP_EDGE",EDGE,{"disambiguationData":[OSD([sQuery(id+"F2.wireOp",EDGE,"E29.0")])],"isStart":false})});
            var Q9;
            Q9=makeQuery(id+"F3.boolean.opBoolean","COPY",EDGE,{"derivedFrom":makeQuery(id+"F3.opExtrude","CAP_EDGE",EDGE,{"disambiguationData":[OSD([sQuery(id+"F2.wireOp",EDGE,"E30.0")])],"isStart":false})});
            var Q10;
            Q10=makeQuery(id+"F3.boolean.opBoolean","COPY",EDGE,{"derivedFrom":makeQuery(id+"F3.opExtrude","CAP_EDGE",EDGE,{"disambiguationData":[OSD([sQuery(id+"F2.wireOp",EDGE,"E26.1")])],"isStart":false})});
            var Q11;
            Q11=makeQuery(id+"F3.boolean.opBoolean","COPY",EDGE,{"derivedFrom":makeQuery(id+"F3.opExtrude","CAP_EDGE",EDGE,{"disambiguationData":[OSD([sQuery(id+"F2.wireOp",EDGE,"E27.0")])],"isStart":false})});
            var Q12;
            Q12=makeQuery(id+"F3.boolean.opBoolean","COPY",EDGE,{"derivedFrom":makeQuery(id+"F3.opExtrude","CAP_EDGE",EDGE,{"disambiguationData":[OSD([sQuery(id+"F2.wireOp",EDGE,"E28.1")])],"isStart":false})});
            var Q13;
            Q13=makeQuery(id+"F3.boolean.opBoolean","COPY",EDGE,{"derivedFrom":makeQuery(id+"F3.opExtrude","CAP_EDGE",EDGE,{"disambiguationData":[OSD([sQuery(id+"F2.wireOp",EDGE,"E29.1")])],"isStart":false})});
            var Q14;
            Q14=makeQuery(id+"F3.boolean.opBoolean","COPY",EDGE,{"derivedFrom":makeQuery(id+"F3.opExtrude","CAP_EDGE",EDGE,{"disambiguationData":[OSD([sQuery(id+"F2.wireOp",EDGE,"E30.1")])],"isStart":false})});
            var Q15;
            Q15=makeQuery(id+"F3.boolean.opBoolean","COPY",EDGE,{"derivedFrom":makeQuery(id+"F3.opExtrude","CAP_EDGE",EDGE,{"disambiguationData":[OSD([sQuery(id+"F2.wireOp",EDGE,"E28.0")])],"isStart":false})});
            fillet(context, id + "F7", {"entities" : qUnion([Q0, Q1, Q2, Q3, Q4, Q5, Q6, Q7, Q8, Q9, Q10, Q11, Q12, Q13, Q14, Q15]), "radius" : 0.5 * mm, "tangentPropagation" : true, "allowEdgeOverflow" : false});
        }
    });
